# Revit family: Lighting-Industriale-GEWISS-SMART[4]HACCP_APPARECCHI-LED_2M
name_source: partatom
category: Apparecchi per illuminazione
units: mm (PartAtom-declared; Revit-internal decimal feet)

## family parameters
Basato su piano di lavoro = Sì
Condiviso = No
Numero OmniClass = 23.80.70.00
Punto di calcolo locali = No
Quota connettore circolare = Usa diametro
Sempre verticale = No
Sorgente d'illuminazione = No
Taglio con vuoti quando caricato = No
Tipo di parte = Normale
Titolo OmniClass = Lighting

## types (1)
- Lighting-Industriale-GEWISS-SMART[4]HACCP_APPARECCHI-LED_2M
    Alimentatore = Incluso
    Apparecchio a ridotta temperatura superficiale = Si
    Applicazione = Interno
    Cablaggio = Con connettore stagno Gw connect
    Caratteristiche elettriche e gestione della luce = -
    Caratteristiche ottiche e illuminotecniche = -
    Carico apparente = 97 VA
    Catalogo = LIGHTING
    Certificazione DIN 18032-3 = -
    Certificazioni e classificazioni = -
    Classe fotobiologica = RG0
    Classe isolamento = I
    Classificazione = Lighting
    Classificazione: = -
    Codice Electrocod = 2444
    Codice digitale univoco (Datamatrix) = Datamatrix
    Colore = Grigio RAL 7035
    Commenti sul wattaggio = 97W
    Contesto = Illuminazione di logistiche e locali produttivi industriali di tipo alimentari
    Controllo abbagliamento e luminanza = -
    Corpo = PA6 “Halogen Free” caricato fibra vetro
    Descrizione = SMART[4]HB 2M S.A.ON/OFF HACCP ELL.57K
    Dispositivo di protezione = DM 6 kV / CM 10 kV
    Dist_sorg_lum = 10 mm  [stored 0.0328084 ft]
    Durata di vita = L90B10 (Tq+25°C) = 70.000 h - L90B10 (Tq+50°C) = 35.000 h
    Efficienza luminosa (lm/W) = 128
    Finitura colore = Grigio RAL 7035
    Fissaggio = -
    Frequenza nominale (Hz) = 50/60 Hz
    Gancio di chiusura = -
    Garanzia = 5 anni
    Grado di protezione = IP65
    Gruppo ottico = Riflettore in PC metallizzato e lenti in PMMA
    Guarnizioni = tipo siliconico antinvecchiamento
    IDF = d06013c2-3bd3-4c85-9af7-b963c25f9889
    IDT = 2f4286e1b10c42c6bc2a92e840e0f90a
    IPEA = -
    Immagine tipo = GWL1311.jpg
    Inclinazione = Con accessorio staffa
    Indice di resa cromatica = CRI-80
    Informazioni generali = -
    Installazione e manutenzione = -
    Lampada = LED
    Larghezza = 254 mm  [stored 0.833333 ft]
    Lumen output (lm) = 16000
    Lunghezza = 699 mm  [stored 2.29331 ft]
    Mascherina = <Per categoria>
    Materiali = -
    Modello = GWS4220HQ857
    Motore = <Per categoria>
    Norma di riferimento = EN 60598-1 ; EN 60598-2-1 ; EN 60598-2-24
    Ottica = Ellittica
    Peso (kg): = 6,5
    Potenza di sistema = 125W
    Produttore = GEWISS S.p.A.
    Prospetto di default = 1219 mm
    Resistenza agli urti = IK07
    Resistenza al filo incandescente = 650 °C
    SEO = High bay
    Scheda Tecnica = https://www.gewiss.com
    Schermo = PMMA
    Sistema di controllo = ON / OFF
    Sistema di controllo : = ON / OFF
    Sostituibilità gruppo ottico = Non sostituibile
    Sostituibilità piastra di cablaggio = Non sostituibile
    Spessore plafoniera = 40 mm  [stored 0.131234 ft]
    Struttura plafoniera = <Per categoria>
    Superficie massima esposta al vento : = 0,184 m²
    Temperatura di colore = 5700K
    Temperatura di esercizio = -30 +50 °C
    Temperatura di stoccaggio = -40 +70 °C
    Tensione di alimentazione = 220 - 240 V
    Tipo di apparecchio = Riflettore industriale a LED&nbsp;
    Tipo di installazione e montaggio = Plafone - Parete - Sospensione
    Tipologia sorgente luminosa = LED - Non sostituibile
    Tolleranza cromatica = SDCM = 3
    Trasformatore = <Per categoria>
    URL = https://www.gewiss.com
    Vano di alimentazione = Integrato
    Versione file RFA = 20.11
    Viti esterne = Acciaio inox
    Voltaggio = 230 V

note: [stored X ft] marks values corroborated as IEEE doubles in the binary element streams (Revit-internal decimal feet)

## geometry (parser evidence)
native form markers: Blend x4, Sweep x2
no freeform markers — native parametric forms only
